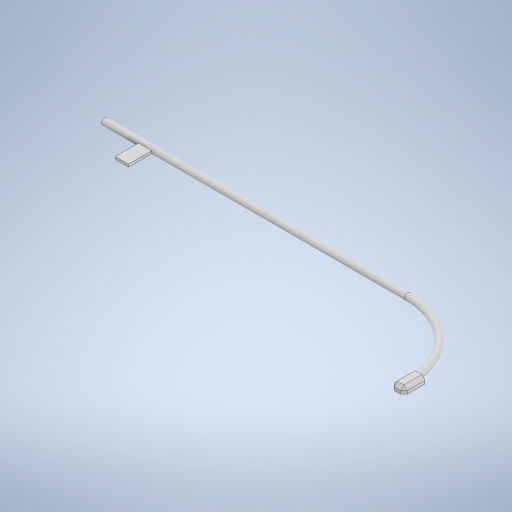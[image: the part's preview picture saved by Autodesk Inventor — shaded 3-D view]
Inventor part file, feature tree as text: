
AUTODESK INVENTOR PART (.ipt)
format: ipt  version: 2023 (Build 270158030, 158C)  size: 279,040 bytes
history: native  units: in
note: dims shown in document units (in); Inventor stores cm internally (conversion verified against a paired STEP export)
features: sketch x4, extrude x2, sweep x1, chamfer x1
ambient origin geometry x8: Origin, YZ Plane, XZ Plane, XY Plane, X Axis, Y Axis, Z Axis, Center Point
bodies: Solid1 (feature_tree)
feature tree (8):
  sweep  "Sweep1"
  extrude  "Extrusion1"  TaperAngle=135.0deg  [1 undecoded]
  chamfer  "Chamfer1"  [1 undecoded]
  extrude  "Extrusion2"  Depth=0.5in
  sketch  "Sketch1"  dims[d0=0.25in d1=11.5in]
  sketch  "Sketch2"  dims[d2=4.0in d3=135.0deg d4=0.0in d5=0.0in]
  sketch  "Sketch3"  dims[d6=0.5in d7=0.8in]
  sketch  "Sketch4"  dims[d8=0.25in d9=0.0in d10=0.125in d11=0.125in d12=45.0deg d13=0.1in d14=3.1in d15=0.5in d16=2.0in d17=0.1in d18=0.0in]
note: 2 required parameter values undecoded (feature->parameter linkage not recoverable at this tier; creation-order binding heuristic only, values carry confidence <= 0.55)
